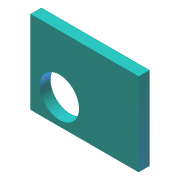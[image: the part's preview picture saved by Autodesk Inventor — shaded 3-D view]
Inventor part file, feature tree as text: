
AUTODESK INVENTOR PART (.ipt)
format: ipt  version: 2012 (Build 160160000, 160)  size: 76,288 bytes
history: native  units: in
note: dims shown in document units (in); Inventor stores cm internally (conversion verified against a paired STEP export)
features: extrude x1, sketch x1
ambient origin geometry x8: Origin, YZ Plane, XZ Plane, XY Plane, X Axis, Y Axis, Z Axis, Center Point
bodies: Solid1 (feature_tree)
feature tree (2):
  extrude  "Extrusion1"  Depth=30.0in
  sketch  "Sketch1"  dims[d0=23.0in d1=30.0in d2=11.0in d3=7.0in d4=8.0in d5=3.0in d6=0.0in]
